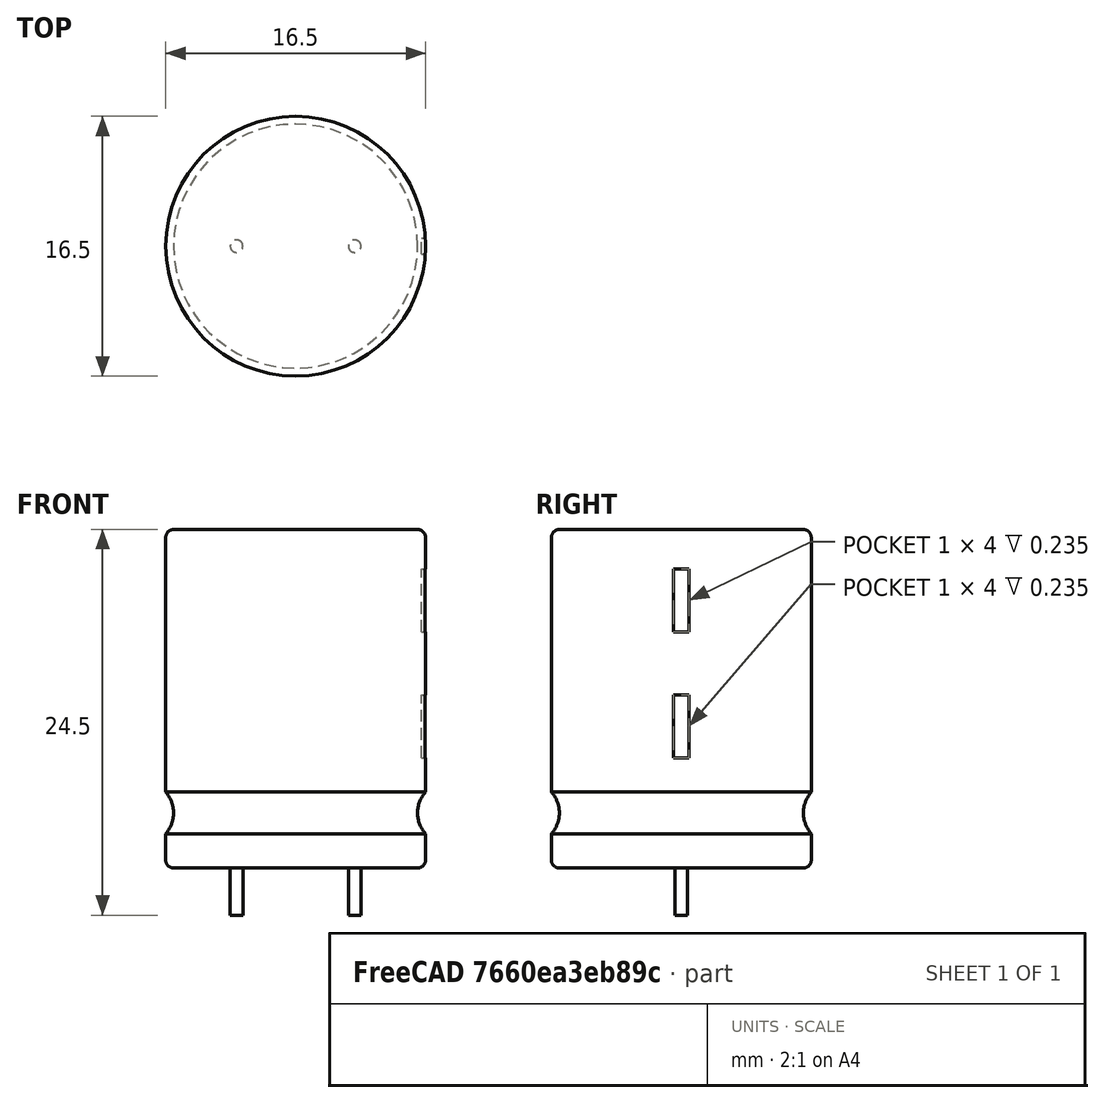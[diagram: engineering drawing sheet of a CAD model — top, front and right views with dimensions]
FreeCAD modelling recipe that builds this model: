
FCSTD DOCUMENT
Label: CAPPR750W80D1600H2000
objects: Part::Cylinder×3, Part::Cut×3, Part::Box×2, Part::Fuse×2, Part::Fillet×1, Part::Torus×1
note: 12 computed .brp shape members not serialized (recipe doc carries the construction recipe); baked Part::Feature solids carry a one-line shape summary decoded from their .brp

FEATURE [Part::Cylinder] Cylinder  label="Grundkoerper"
  Angle = 360
  Height = 21.5
  Radius = 8.25
FEATURE [Part::Cylinder] Cylinder001  label="Pin1+"
  Angle = 360
  Height = 3
  Placement = pos=(-3.75,0,-3) rot=(0,0,1;0rad)
  Radius = 0.4
FEATURE [Part::Cylinder] Cylinder002  label="Pin2-"
  Angle = 360
  Height = 3
  Placement = pos=(3.75,0,-3) rot=(0,0,1;0rad)
  Radius = 0.4
FEATURE [Part::Fillet] Fillet  label="Abgerundeter Grundkoerper"
  Base = -> Cylinder
  Edges = 2 edges r=0.5: [Edge1,Edge3]
FEATURE [Part::Torus] Torus  label="Ring"
  Angle1 = -180
  Angle2 = 180
  Angle3 = 360
  Placement = pos=(0,0,3.5) rot=(0,0,1;0rad)
  Radius1 = 9.75
  Radius2 = 2
FEATURE [Part::Cut] Cut  label="Beringter kondensator"
  Base = -> Fillet
  Tool = -> Torus
FEATURE [Part::Box] Box
  Height = 4
  Length = 1
  Placement = pos=(8,-0.5,7) rot=(0,0,1;0rad)
  Width = 1
FEATURE [Part::Box] Box001
  Height = 4
  Length = 1
  Placement = pos=(8,-0.5,15) rot=(0,0,1;0rad)
  Width = 1
FEATURE [Part::Cut] Cut001
  Base = -> Cut
  Tool = -> Box
FEATURE [Part::Cut] Cut002
  Base = -> Cut001
  Tool = -> Box001
FEATURE [Part::Fuse] Fusion
  Base = -> Cut002
  Tool = -> Cylinder001
FEATURE [Part::Fuse] Fusion001  label="CAPPR750W80D1600H2000"
  Base = -> Fusion
  Tool = -> Cylinder002
